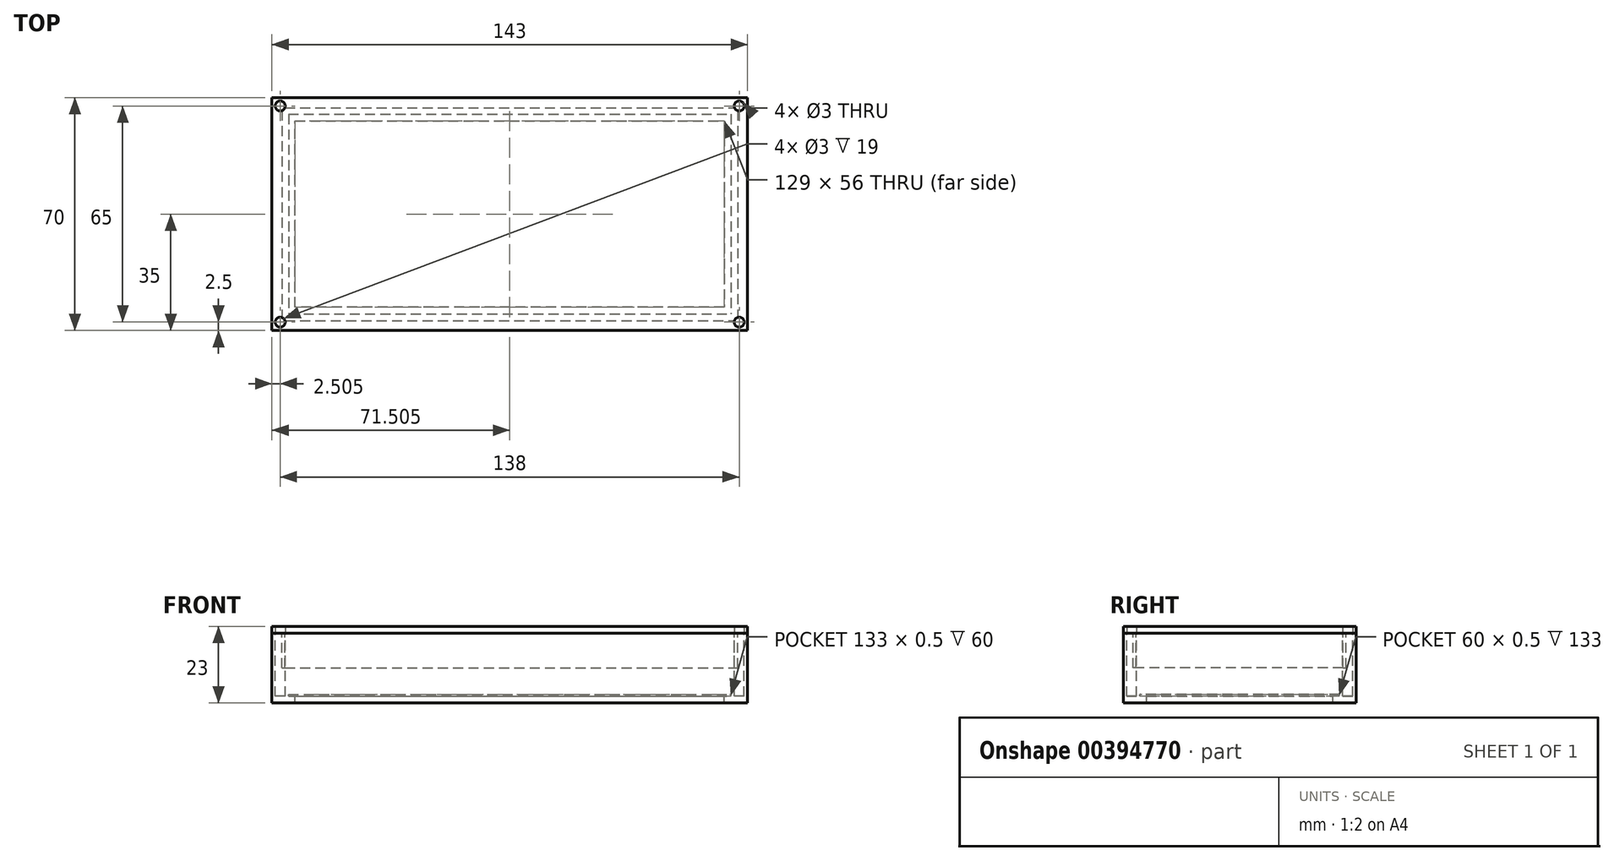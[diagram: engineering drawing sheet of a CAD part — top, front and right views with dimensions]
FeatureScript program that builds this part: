
annotation { "Feature Type Name" : "Feature", "Feature Type Description" : "" }
export const myFeature = defineFeature(function(context is Context, id is Id, definition is map)
    precondition{}
    {
        {
            var Q0;
            Q0=qCreatedBy(makeId("Top.planeOp"),FACE);
            var sketch = newSketch(context, id + "F0", { "sketchPlane" : qUnion([Q0])});
            skLineSegment(sketch, "E0.bottom", {"start": v(-63.48, 30) * mm, "end": v(69.52, 30) * mm});
            skLineSegment(sketch, "E0.top", {"start": v(-63.48, -30) * mm, "end": v(69.52, -30) * mm});
            skLineSegment(sketch, "E0.left", {"start": v(-63.48, 30) * mm, "end": v(-63.48, -30) * mm});
            skLineSegment(sketch, "E0.right", {"start": v(69.52, 30) * mm, "end": v(69.52, -30) * mm});
            skLineSegment(sketch, "E1.0", {"start": v(-68.48, 35) * mm, "end": v(-68.48, -35) * mm});
            skLineSegment(sketch, "E1.1", {"start": v(-68.48, 35) * mm, "end": v(74.52, 35) * mm});
            skLineSegment(sketch, "E1.2", {"start": v(74.52, 35) * mm, "end": v(74.52, -35) * mm});
            skLineSegment(sketch, "E1.3", {"start": v(-68.48, -35) * mm, "end": v(74.52, -35) * mm});
            skLineSegment(sketch, "E2.0", {"start": v(-65.98, 32.5) * mm, "end": v(72.02, 32.5) * mm, "construction": true});
            skLineSegment(sketch, "E2.1", {"start": v(-65.98, 32.5) * mm, "end": v(-65.98, -32.5) * mm, "construction": true});
            skLineSegment(sketch, "E2.2", {"start": v(-65.98, -32.5) * mm, "end": v(72.02, -32.5) * mm, "construction": true});
            skLineSegment(sketch, "E2.3", {"start": v(72.02, 32.5) * mm, "end": v(72.02, -32.5) * mm, "construction": true});
            skCircle(sketch, "E3", {"center": v(-65.98, 32.5) * mm, "radius": 1.5 * mm});
            skCircle(sketch, "E4", {"center": v(72.02, 32.5) * mm, "radius": 1.5 * mm});
            skCircle(sketch, "E5", {"center": v(72.02, -32.5) * mm, "radius": 1.5 * mm});
            skCircle(sketch, "E6", {"center": v(-65.98, -32.5) * mm, "radius": 1.5 * mm});
            skSolve(sketch);
        }
        {
            var Q0;
            Q0=makeQuery(id+"F0.imprint","IMPRINT",FACE,{"disambiguationData":[TD([[makeQuery(id+"F0.imprint","IMPRINT",EDGE,{"derivedFrom":sQuery(id+"F0.wireOp",EDGE,"E0.bottom")}),-1.0]])]});
            extrude(context, id + "F1", {"entities" : qUnion([Q0]), "oppositeDirection" : true, "depth" : 8 * mm});
        }
        {
            var Q0;
            Q0=makeQuery(id+"F0.imprint","IMPRINT",FACE,{"disambiguationData":[TD([[makeQuery(id+"F0.imprint","IMPRINT",EDGE,{"derivedFrom":sQuery(id+"F0.wireOp",EDGE,"E0.bottom")}),1.0]])]});
            extrude(context, id + "F2", {"entities" : qUnion([Q0]), "oppositeDirection" : true, "depth" : 8.5 * mm});
        }
        {
            var Q0;
            Q0=makeQuery(id+"F2.opExtrude","CAP_FACE",FACE,{"disambiguationData":[OSD([sQuery(id+"F0.wireOp",EDGE,"E0.bottom"),sQuery(id+"F0.wireOp",EDGE,"E0.top"),sQuery(id+"F0.wireOp",EDGE,"E0.left"),sQuery(id+"F0.wireOp",EDGE,"E0.right"),sQuery(id+"F0.wireOp",EDGE,"E1.0"),sQuery(id+"F0.wireOp",EDGE,"E1.1"),sQuery(id+"F0.wireOp",EDGE,"E1.2"),sQuery(id+"F0.wireOp",EDGE,"E1.3"),sQuery(id+"F0.wireOp",EDGE,"E3"),sQuery(id+"F0.wireOp",EDGE,"E4"),sQuery(id+"F0.wireOp",EDGE,"E5"),sQuery(id+"F0.wireOp",EDGE,"E6")])],"isStart":false});
            var sketch = newSketch(context, id + "F3", { "sketchPlane" : qUnion([Q0])});
            skLineSegment(sketch, "E7.bottom", {"start": v(-68.48, 35) * mm, "end": v(74.52, 35) * mm});
            skLineSegment(sketch, "E7.top", {"start": v(-68.48, -35) * mm, "end": v(74.52, -35) * mm});
            skLineSegment(sketch, "E7.left", {"start": v(-68.48, 35) * mm, "end": v(-68.48, -35) * mm});
            skLineSegment(sketch, "E7.right", {"start": v(74.52, 35) * mm, "end": v(74.52, -35) * mm});
            skLineSegment(sketch, "E8.0", {"start": v(-61.48, 28) * mm, "end": v(-61.48, -28) * mm});
            skLineSegment(sketch, "E8.1", {"start": v(67.52, 28) * mm, "end": v(-61.48, 28) * mm});
            skLineSegment(sketch, "E8.2", {"start": v(67.52, -28) * mm, "end": v(67.52, 28) * mm});
            skLineSegment(sketch, "E8.3", {"start": v(-61.48, -28) * mm, "end": v(67.52, -28) * mm});
            skSolve(sketch);
        }
        {
            var Q0;
            Q0 = qSketchRegion(id + "F3", true);
            extrude(context, id + "F4", {"entities" : qUnion([Q0]), "operationType" : NewBodyOperationType.ADD, "depth" : 2 * mm});
        }
        {
            var Q0;
            Q0=makeQuery(id+"F0.imprint","IMPRINT",FACE,{"disambiguationData":[TD([[makeQuery(id+"F0.imprint","IMPRINT",EDGE,{"derivedFrom":sQuery(id+"F0.wireOp",EDGE,"E0.bottom")}),1.0]])]});
            var Q1;
            Q1 = qSketchRegion(id + "F6", true);
            extrude(context, id + "F5", {"entities" : qUnion([Q0, Q1]), "operationType" : NewBodyOperationType.ADD, "depth" : 10.5 * mm});
        }
        {
            var Q0;
            Q0=makeQuery(id+"F5.opExtrude","CAP_FACE",FACE,{"disambiguationData":[OSD([sQuery(id+"F0.wireOp",EDGE,"E0.bottom"),sQuery(id+"F0.wireOp",EDGE,"E0.top"),sQuery(id+"F0.wireOp",EDGE,"E0.left"),sQuery(id+"F0.wireOp",EDGE,"E0.right"),sQuery(id+"F0.wireOp",EDGE,"E1.0"),sQuery(id+"F0.wireOp",EDGE,"E1.1"),sQuery(id+"F0.wireOp",EDGE,"E1.2"),sQuery(id+"F0.wireOp",EDGE,"E1.3"),sQuery(id+"F0.wireOp",EDGE,"E3"),sQuery(id+"F0.wireOp",EDGE,"E4"),sQuery(id+"F0.wireOp",EDGE,"E5"),sQuery(id+"F0.wireOp",EDGE,"E6")])],"isStart":false});
            var sketch = newSketch(context, id + "F6", { "sketchPlane" : qUnion([Q0])});
            skLineSegment(sketch, "E9.bottom", {"start": v(-68.48, 35) * mm, "end": v(74.52, 35) * mm});
            skLineSegment(sketch, "E9.top", {"start": v(-68.48, -35) * mm, "end": v(74.52, -35) * mm});
            skLineSegment(sketch, "E9.left", {"start": v(-68.48, 35) * mm, "end": v(-68.48, -35) * mm});
            skLineSegment(sketch, "E9.right", {"start": v(74.52, 35) * mm, "end": v(74.52, -35) * mm});
            skLineSegment(sketch, "E10.0", {"start": v(-65.48, 32) * mm, "end": v(-65.48, -32) * mm});
            skLineSegment(sketch, "E10.1", {"start": v(-65.48, 32) * mm, "end": v(71.52, 32) * mm});
            skLineSegment(sketch, "E10.2", {"start": v(71.52, 32) * mm, "end": v(71.52, -32) * mm});
            skLineSegment(sketch, "E10.3", {"start": v(-65.48, -32) * mm, "end": v(71.52, -32) * mm});
            skSolve(sketch);
        }
        {
            var Q0;
            Q0=makeQuery(id+"F6.imprint","IMPRINT",FACE,{"disambiguationData":[TD([[makeQuery(id+"F6.imprint","IMPRINT",EDGE,{"derivedFrom":makeQuery(id+"F5.opExtrude","CAP_EDGE",EDGE,{"disambiguationData":[OSD([sQuery(id+"F0.wireOp",EDGE,"E0.bottom")])],"isStart":false})}),1.0]])]});
            extrude(context, id + "F7", {"entities" : qUnion([Q0]), "operationType" : NewBodyOperationType.REMOVE, "oppositeDirection" : true, "depth" : 10.5 * mm});
        }
        {
            var Q0;
            Q0=makeQuery(id+"F5.opExtrude","CAP_FACE",FACE,{"disambiguationData":[OSD([sQuery(id+"F0.wireOp",EDGE,"E0.bottom"),sQuery(id+"F0.wireOp",EDGE,"E0.top"),sQuery(id+"F0.wireOp",EDGE,"E0.left"),sQuery(id+"F0.wireOp",EDGE,"E0.right"),sQuery(id+"F0.wireOp",EDGE,"E1.0"),sQuery(id+"F0.wireOp",EDGE,"E1.1"),sQuery(id+"F0.wireOp",EDGE,"E1.2"),sQuery(id+"F0.wireOp",EDGE,"E1.3"),sQuery(id+"F0.wireOp",EDGE,"E3"),sQuery(id+"F0.wireOp",EDGE,"E4"),sQuery(id+"F0.wireOp",EDGE,"E5"),sQuery(id+"F0.wireOp",EDGE,"E6")])],"isStart":false});
            var sketch = newSketch(context, id + "F8", { "sketchPlane" : qUnion([Q0])});
            skLineSegment(sketch, "E11.bottom", {"start": v(-68.48, 35) * mm, "end": v(74.52, 35) * mm});
            skLineSegment(sketch, "E11.top", {"start": v(-68.48, -35) * mm, "end": v(74.52, -35) * mm});
            skLineSegment(sketch, "E11.left", {"start": v(-68.48, 35) * mm, "end": v(-68.48, -35) * mm});
            skLineSegment(sketch, "E11.right", {"start": v(74.52, 35) * mm, "end": v(74.52, -35) * mm});
            skCircle(sketch, "E12", {"center": v(-65.98, 32.5) * mm, "radius": 1.5 * mm});
            skCircle(sketch, "E13", {"center": v(72.02, 32.5) * mm, "radius": 1.5 * mm});
            skCircle(sketch, "E14", {"center": v(72.02, -32.5) * mm, "radius": 1.5 * mm});
            skCircle(sketch, "E15", {"center": v(-65.98, -32.5) * mm, "radius": 1.5 * mm});
            skSolve(sketch);
        }
        {
            var Q0;
            Q0 = qSketchRegion(id + "F8", true);
            extrude(context, id + "F9", {"entities" : qUnion([Q0]), "depth" : 2 * mm});
        }
    });
